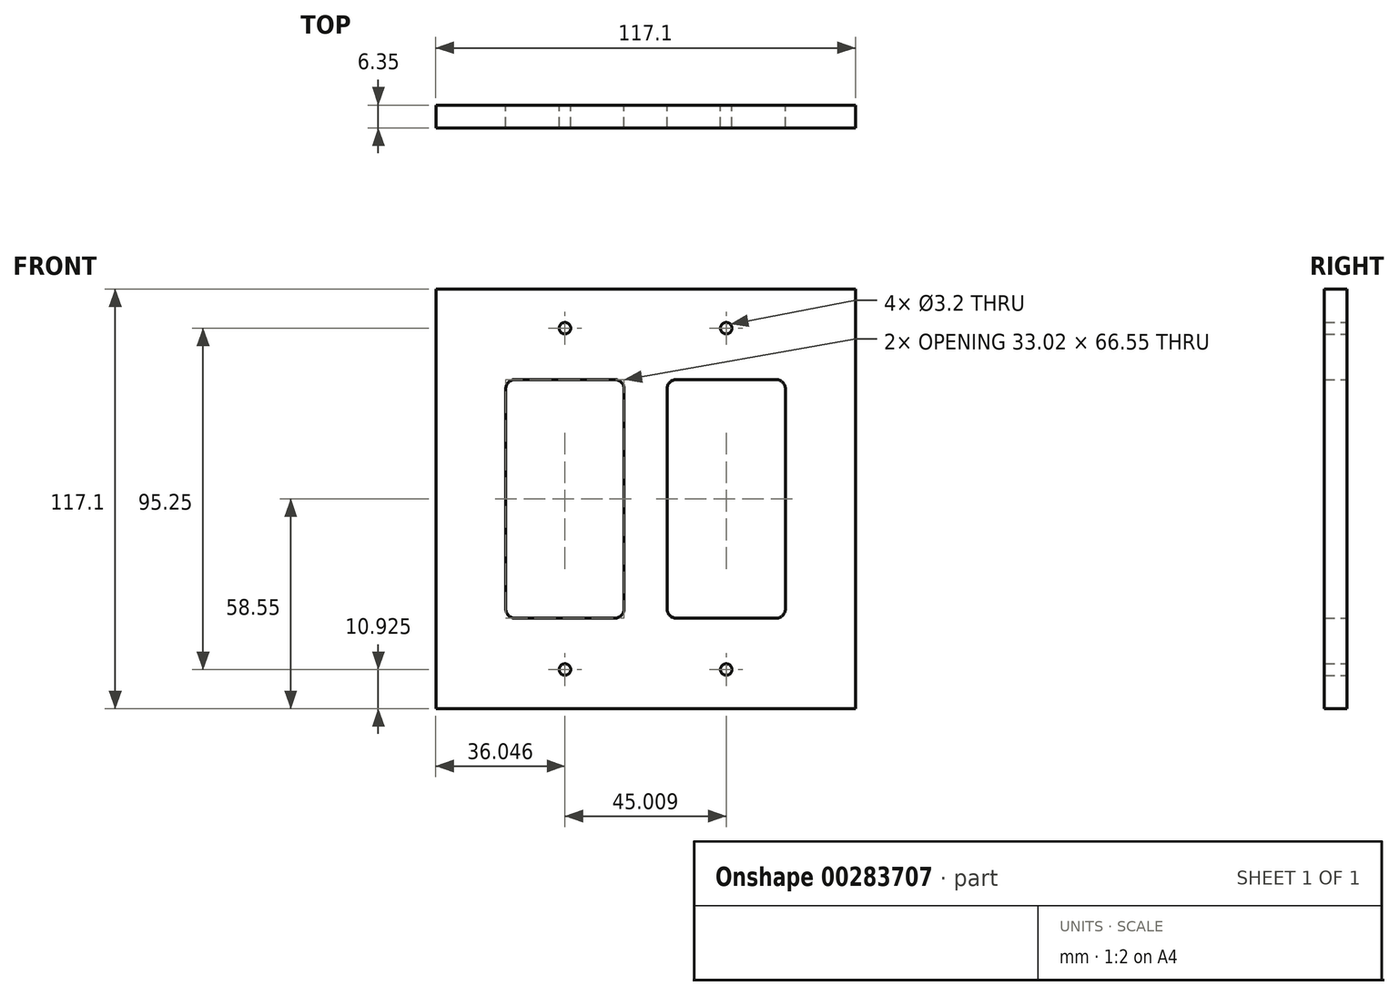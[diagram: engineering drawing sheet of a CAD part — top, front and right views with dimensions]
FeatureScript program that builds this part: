
annotation { "Feature Type Name" : "Feature", "Feature Type Description" : "" }
export const myFeature = defineFeature(function(context is Context, id is Id, definition is map)
    precondition{}
    {
        {
            var Q0;
            Q0=qCreatedBy(makeId("Front.planeOp"),FACE);
            var sketch = newSketch(context, id + "F0", { "sketchPlane" : qUnion([Q0])});
            skLineSegment(sketch, "E0.bottom", {"start": v(0, 58.55) * mm, "end": v(58.55, 58.55) * mm});
            skLineSegment(sketch, "E0.right", {"start": v(58.55, 58.55) * mm, "end": v(58.55, 0) * mm});
            skLineSegment(sketch, "E1.bottom", {"start": v(6, 33.27) * mm, "end": v(39.01, 33.27) * mm});
            skLineSegment(sketch, "E1.left", {"start": v(6, 33.27) * mm, "end": v(6, 0) * mm});
            skLineSegment(sketch, "E1.right", {"start": v(39.01, 33.27) * mm, "end": v(39.01, 0) * mm});
            skCircle(sketch, "E2", {"center": v(22.5, 47.63) * mm, "radius": 1.6 * mm});
            skLineSegment(sketch, "E3", {"start": v(-72.1, 0) * mm, "end": v(76.29, 0) * mm, "construction": true});
            skLineSegment(sketch, "E4", {"start": v(0, -63.26) * mm, "end": v(0, 62.33) * mm, "construction": true});
            skLineSegment(sketch, "E5", {"start": v(22.5, 33.27) * mm, "end": v(22.5, 62.11) * mm, "construction": true});
            skCircle(sketch, "E6.MirrorC", {"center": v(-22.5, 47.63) * mm, "radius": 1.6 * mm});
            skLineSegment(sketch, "E7.MirrorCS", {"start": v(-6, 33.27) * mm, "end": v(-6, 0) * mm});
            skLineSegment(sketch, "E8.MirrorCS", {"start": v(72.1, 0) * mm, "end": v(-76.29, 0) * mm, "construction": true});
            skLineSegment(sketch, "E9.MirrorCS", {"start": v(-22.5, 33.27) * mm, "end": v(-22.5, 62.11) * mm, "construction": true});
            skLineSegment(sketch, "E10.MirrorCS", {"start": v(-58.55, 58.55) * mm, "end": v(-58.55, 0) * mm});
            skLineSegment(sketch, "E11.MirrorCS", {"start": v(-39.01, 33.27) * mm, "end": v(-39.01, 0) * mm});
            skLineSegment(sketch, "E12.MirrorCS", {"start": v(-6, 33.27) * mm, "end": v(-39.01, 33.27) * mm});
            skLineSegment(sketch, "E13.MirrorCS", {"start": v(0, 58.55) * mm, "end": v(-58.55, 58.55) * mm});
            skCircle(sketch, "E14.MirrorC", {"center": v(-22.5, -47.63) * mm, "radius": 1.6 * mm});
            skCircle(sketch, "E15.MirrorC", {"center": v(22.5, -47.63) * mm, "radius": 1.6 * mm});
            skLineSegment(sketch, "E16.MirrorCS", {"start": v(0, -58.55) * mm, "end": v(58.55, -58.55) * mm});
            skLineSegment(sketch, "E17.MirrorCS", {"start": v(-22.5, -33.27) * mm, "end": v(-22.5, -62.11) * mm, "construction": true});
            skLineSegment(sketch, "E18.MirrorCS", {"start": v(22.5, -33.27) * mm, "end": v(22.5, -62.11) * mm, "construction": true});
            skLineSegment(sketch, "E19.MirrorCS", {"start": v(-6, -33.27) * mm, "end": v(-6, 0) * mm});
            skLineSegment(sketch, "E20.MirrorCS", {"start": v(6, -33.27) * mm, "end": v(6, 0) * mm});
            skLineSegment(sketch, "E21.MirrorCS", {"start": v(6, -33.27) * mm, "end": v(39.01, -33.27) * mm});
            skLineSegment(sketch, "E22.MirrorCS", {"start": v(-39.01, -33.27) * mm, "end": v(-39.01, 0) * mm});
            skLineSegment(sketch, "E23.MirrorCS", {"start": v(-6, -33.27) * mm, "end": v(-39.01, -33.27) * mm});
            skLineSegment(sketch, "E24.MirrorCS", {"start": v(58.55, -58.55) * mm, "end": v(58.55, 0) * mm});
            skLineSegment(sketch, "E25.MirrorCS", {"start": v(-58.55, -58.55) * mm, "end": v(-58.55, 0) * mm});
            skLineSegment(sketch, "E26.MirrorCS", {"start": v(0, -58.55) * mm, "end": v(-58.55, -58.55) * mm});
            skLineSegment(sketch, "E27.MirrorCS", {"start": v(39.01, -33.27) * mm, "end": v(39.01, 0) * mm});
            skSolve(sketch);
        }
        {
            var Q0;
            Q0 = qSketchRegion(id + "F0", true);
            extrude(context, id + "F1", {"entities" : qUnion([Q0]), "depth" : 6.35 * mm});
        }
        {
            var Q0;
            Q0=makeQuery(id+"F1.opExtrude","SWEPT_EDGE",EDGE,{"disambiguationData":[OSD([sQuery(id+"F0.wireOp",EDGE,"E1.bottom"),sQuery(id+"F0.wireOp",EDGE,"E1.right")])]});
            var Q1;
            Q1=makeQuery(id+"F1.opExtrude","SWEPT_EDGE",EDGE,{"disambiguationData":[OSD([sQuery(id+"F0.wireOp",EDGE,"E21.MirrorCS"),sQuery(id+"F0.wireOp",EDGE,"E27.MirrorCS")])]});
            var Q2;
            Q2=makeQuery(id+"F1.opExtrude","SWEPT_EDGE",EDGE,{"disambiguationData":[OSD([sQuery(id+"F0.wireOp",EDGE,"E19.MirrorCS"),sQuery(id+"F0.wireOp",EDGE,"E23.MirrorCS")])]});
            var Q3;
            Q3=makeQuery(id+"F1.opExtrude","SWEPT_EDGE",EDGE,{"disambiguationData":[OSD([sQuery(id+"F0.wireOp",EDGE,"E7.MirrorCS"),sQuery(id+"F0.wireOp",EDGE,"E12.MirrorCS")])]});
            var Q4;
            Q4=makeQuery(id+"F1.opExtrude","SWEPT_EDGE",EDGE,{"disambiguationData":[OSD([sQuery(id+"F0.wireOp",EDGE,"E1.bottom"),sQuery(id+"F0.wireOp",EDGE,"E1.left")])]});
            var Q5;
            Q5=makeQuery(id+"F1.opExtrude","SWEPT_EDGE",EDGE,{"disambiguationData":[OSD([sQuery(id+"F0.wireOp",EDGE,"E11.MirrorCS"),sQuery(id+"F0.wireOp",EDGE,"E12.MirrorCS")])]});
            var Q6;
            Q6=makeQuery(id+"F1.opExtrude","SWEPT_EDGE",EDGE,{"disambiguationData":[OSD([sQuery(id+"F0.wireOp",EDGE,"E20.MirrorCS"),sQuery(id+"F0.wireOp",EDGE,"E21.MirrorCS")])]});
            var Q7;
            Q7=makeQuery(id+"F1.opExtrude","SWEPT_EDGE",EDGE,{"disambiguationData":[OSD([sQuery(id+"F0.wireOp",EDGE,"E22.MirrorCS"),sQuery(id+"F0.wireOp",EDGE,"E23.MirrorCS")])]});
            fillet(context, id + "F2", {"entities" : qUnion([Q0, Q1, Q2, Q3, Q4, Q5, Q6, Q7]), "radius" : 2.54 * mm, "tangentPropagation" : true, "allowEdgeOverflow" : false});
        }
    });
